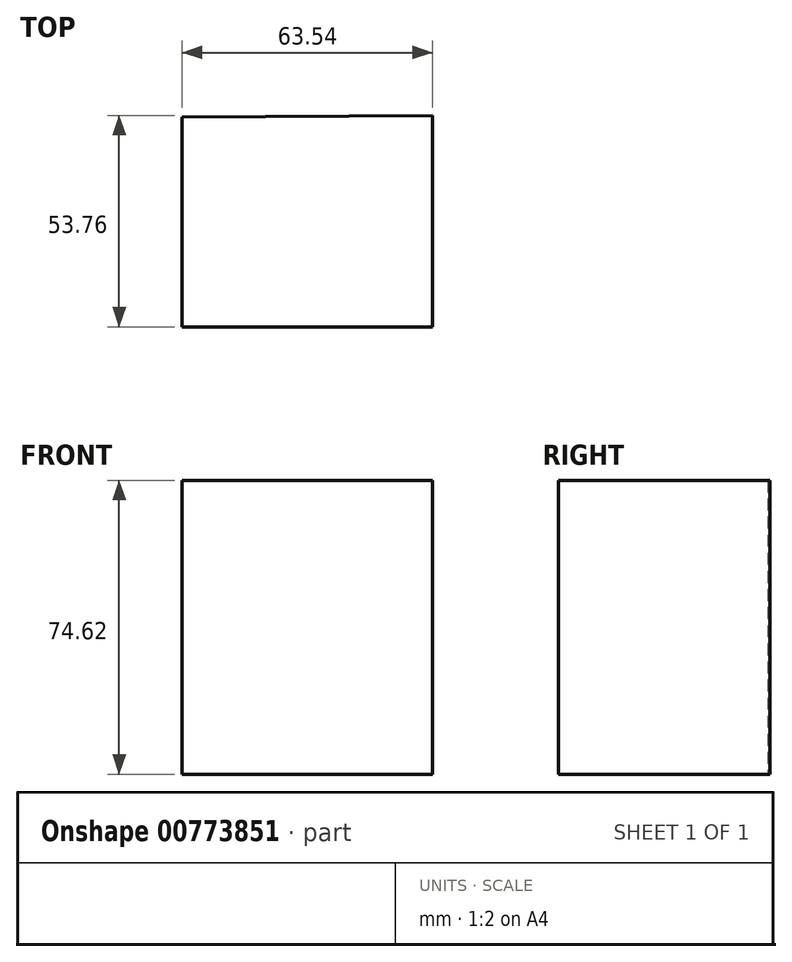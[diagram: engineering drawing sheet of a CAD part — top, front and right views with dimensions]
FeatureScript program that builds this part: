
annotation { "Feature Type Name" : "Feature", "Feature Type Description" : "" }
export const myFeature = defineFeature(function(context is Context, id is Id, definition is map)
    precondition{}
    {
        {
            var Q0;
            Q0=qCreatedBy(makeId("Top.planeOp"),FACE);
            var sketch = newSketch(context, id + "F0", { "sketchPlane" : qUnion([Q0])});
            skPoint(sketch, "E0.start.orphan", {"position": v(-3.93, 0) * mm});
            skLineSegment(sketch, "E1", {"start": v(0, 53.27) * mm, "end": v(0, 0) * mm});
            skLineSegment(sketch, "E2", {"start": v(0, 0) * mm, "end": v(63.54, 0) * mm});
            skLineSegment(sketch, "E3", {"start": v(63.54, 0) * mm, "end": v(63.54, 53.76) * mm});
            skLineSegment(sketch, "E4", {"start": v(63.54, 53.76) * mm, "end": v(0, 53.27) * mm});
            skSolve(sketch);
        }
        {
            var Q0;
            Q0 = qSketchRegion(id + "F0", true);
            extrude(context, id + "F1", {"entities" : qUnion([Q0]), "depth" : 74.62 * mm, "offsetDistance" : 25.4 * mm});
        }
    });
